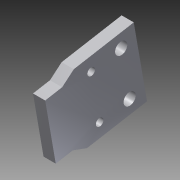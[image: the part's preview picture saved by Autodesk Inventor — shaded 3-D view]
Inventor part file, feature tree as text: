
AUTODESK INVENTOR PART (.ipt)
format: ipt  version: 2013 (Build 170138000, 138)  size: 194,560 bytes
history: native  units: mm
features: sketch x8, extrude x4, hole x4, other x2, pattern_circular x1
ambient origin geometry x8: Origin, YZ Plane, XZ Plane, XY Plane, X Axis, Y Axis, Z Axis, Center Point
feature tree (19):
  other  "ソリッド1"
  extrude  "押し出し1"  Depth=20.0mm
  hole  "穴2"  [1 undecoded]
  extrude  "押し出し2"  Depth=10.0mm
  hole  "穴3"  [1 undecoded]
  hole  "穴4"  [1 undecoded]
  pattern_circular  "円形状パターン3"  [2 undecoded]
  extrude  "押し出し3"  Depth=8.0mm
  hole  "穴5"  [1 undecoded]
  extrude  "押し出し4"  Depth=4.0mm
  sketch  "スケッチ2"
  sketch  "スケッチ4"
  sketch  "スケッチ5"
  sketch  "スケッチ6"
  sketch  "スケッチ7"
  sketch  "スケッチ8"
  sketch  "スケッチ9"
  sketch  "スケッチ10"
  other  "断面エッジを投影1"
note: 6 required parameter values undecoded (feature->parameter linkage not recoverable at this tier; creation-order binding heuristic only, values carry confidence <= 0.55)
